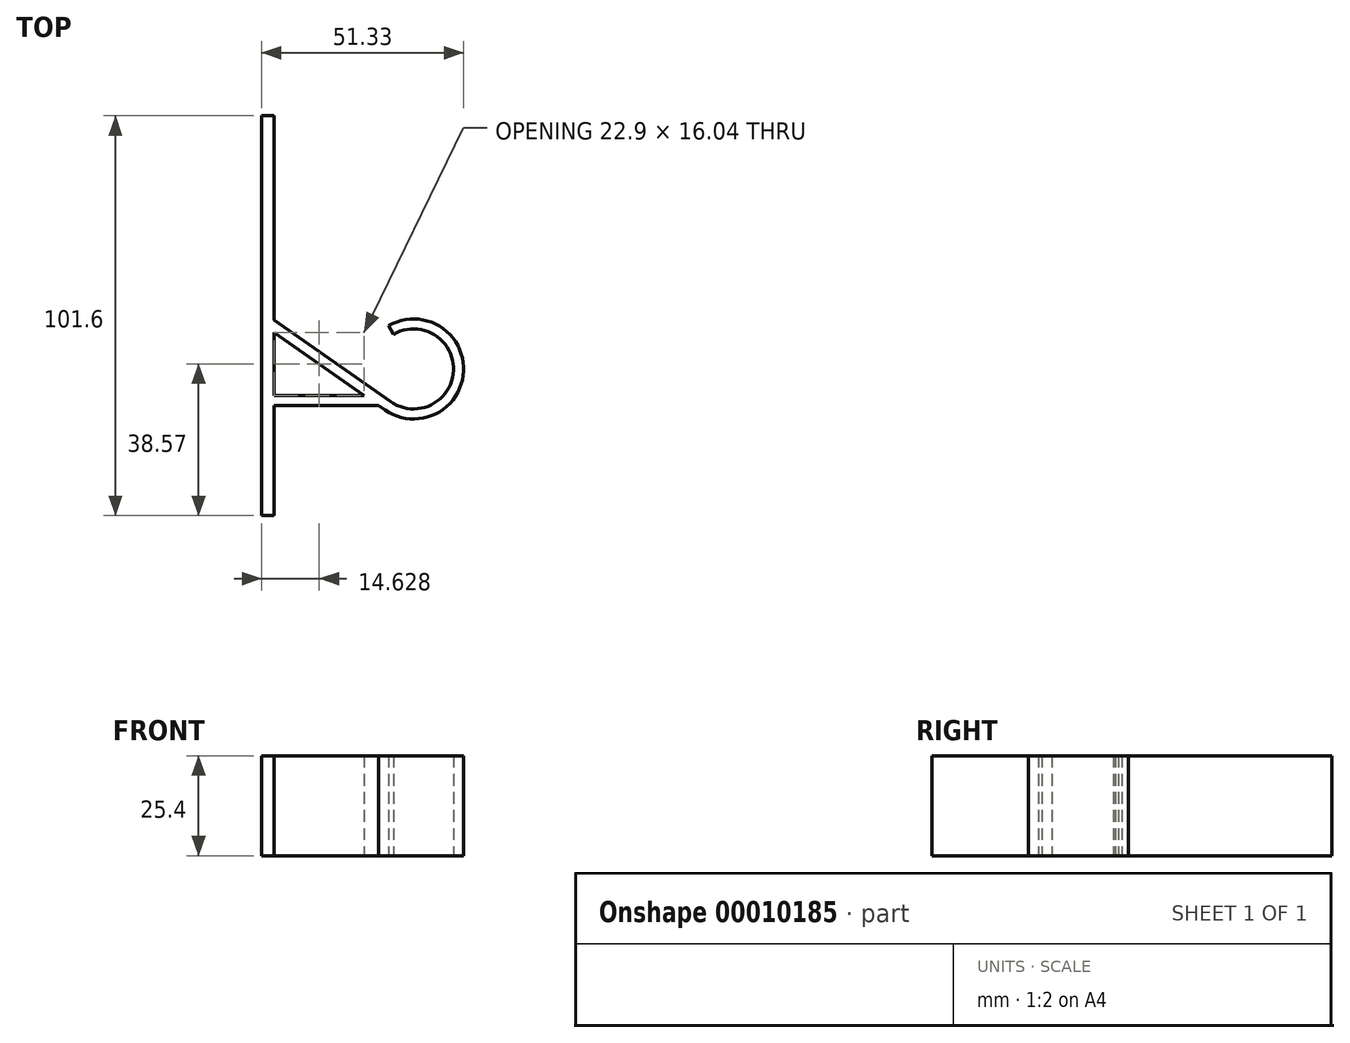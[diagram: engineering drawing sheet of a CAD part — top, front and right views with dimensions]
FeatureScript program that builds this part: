
annotation { "Feature Type Name" : "Feature", "Feature Type Description" : "" }
export const myFeature = defineFeature(function(context is Context, id is Id, definition is map)
    precondition{}
    {
        {
            var Q0;
            Q0=qCreatedBy(makeId("Top.planeOp"),FACE);
            var sketch = newSketch(context, id + "F0", { "sketchPlane" : qUnion([Q0])});
            skLineSegment(sketch, "E0.rect.bottom", {"start": v(1.59, 50.8) * mm, "end": v(-1.59, 50.8) * mm});
            skLineSegment(sketch, "E0.rect.top", {"start": v(1.59, -50.8) * mm, "end": v(-1.59, -50.8) * mm});
            skLineSegment(sketch, "E0.rect.left", {"start": v(1.59, 50.8) * mm, "end": v(1.59, -1.11) * mm});
            skLineSegment(sketch, "E0.rect.right", {"start": v(-1.59, 50.8) * mm, "end": v(-1.59, -50.8) * mm});
            skPoint(sketch, "E0.rect.middle", {"position": v(0, 0) * mm});
            skLineSegment(sketch, "E1", {"start": v(1.59, -1.11) * mm, "end": v(31.2, -21.85) * mm});
            skArc(sketch, "E2", {"start": v(31.2, -21.85) * mm, "mid": v(47.19, -13.97) * mm, "end": v(31.96, -4.73) * mm});
            skLineSegment(sketch, "E3", {"start": v(37.04, -13.53) * mm, "end": v(31.96, -4.73) * mm, "construction": true});
            skArc(sketch, "E4.1", {"start": v(29.75, -23.93) * mm, "mid": v(49.73, -14.08) * mm, "end": v(30.69, -2.53) * mm});
            skLineSegment(sketch, "E4.2", {"start": v(1.59, -4.21) * mm, "end": v(24.49, -20.25) * mm});
            skLineSegment(sketch, "E5", {"start": v(31.96, -4.73) * mm, "end": v(30.69, -2.53) * mm});
            skPoint(sketch, "E6", {"position": v(1.59, -1.11) * mm});
            skLineSegment(sketch, "E7.trimOffspring", {"start": v(1.59, -4.21) * mm, "end": v(1.59, -20.25) * mm});
            skLineSegment(sketch, "E8", {"start": v(1.59, -22.79) * mm, "end": v(28.12, -22.79) * mm});
            skLineSegment(sketch, "E9.0", {"start": v(1.59, -20.25) * mm, "end": v(24.49, -20.25) * mm});
            skPoint(sketch, "E10", {"position": v(24.49, -20.25) * mm});
            skLineSegment(sketch, "E11.trimOffspring", {"start": v(28.12, -22.79) * mm, "end": v(29.75, -23.93) * mm});
            skLineSegment(sketch, "E12.trimOffspring", {"start": v(1.59, -22.79) * mm, "end": v(1.59, -50.8) * mm});
            skSolve(sketch);
        }
        {
            var Q0;
            Q0 = qSketchRegion(id + "F0", true);
            extrude(context, id + "F1", {"entities" : qUnion([Q0]), "depth" : 25.4 * mm});
        }
    });
